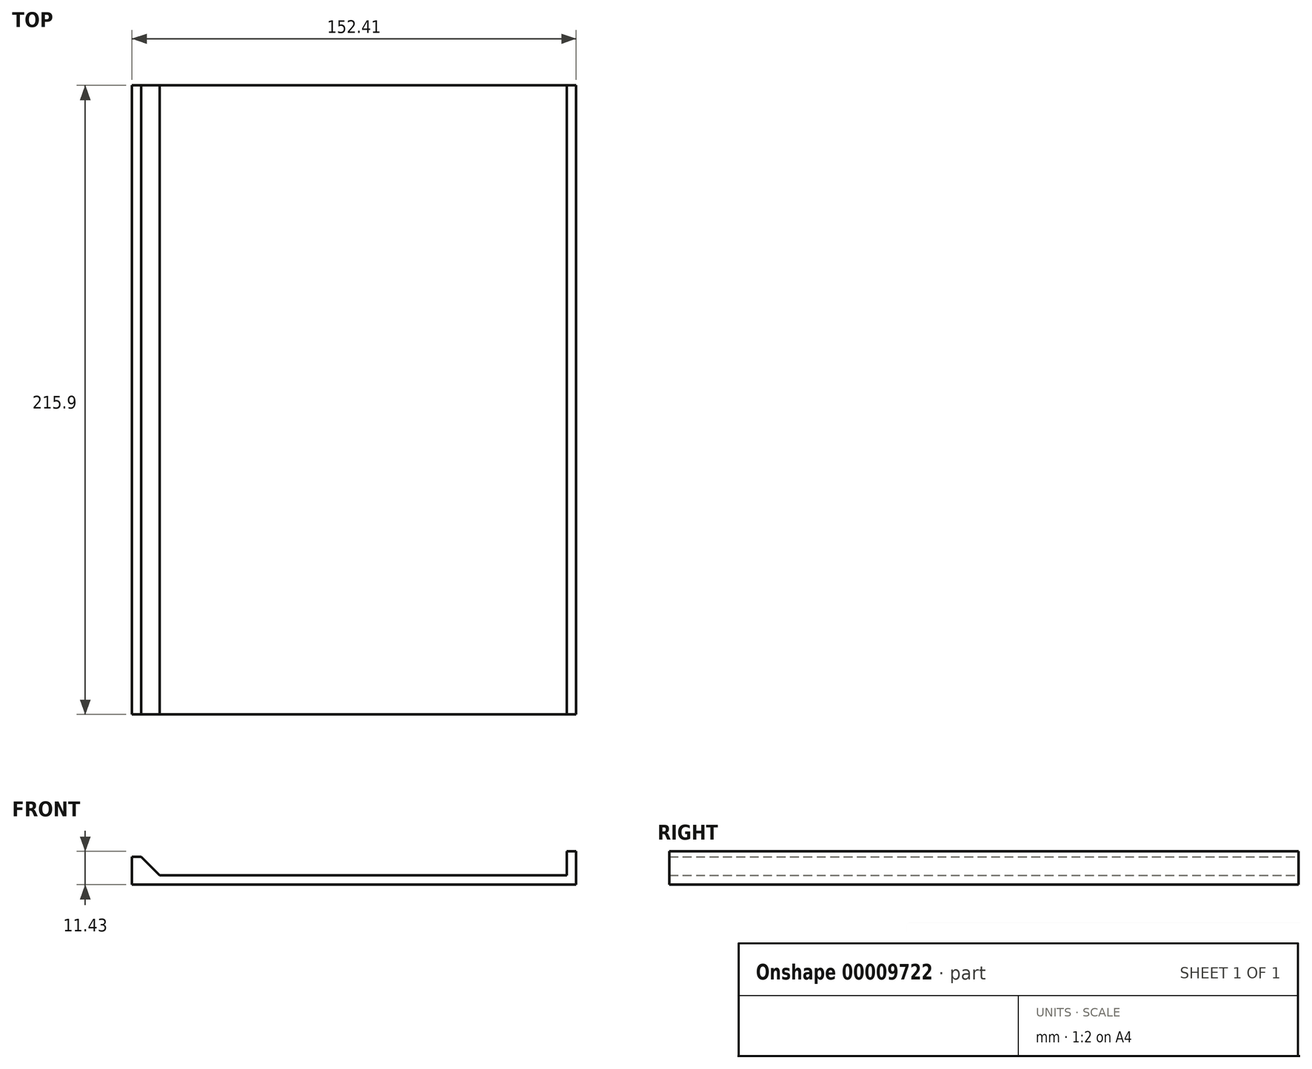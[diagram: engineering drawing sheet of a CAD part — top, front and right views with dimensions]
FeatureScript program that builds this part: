
annotation { "Feature Type Name" : "Feature", "Feature Type Description" : "" }
export const myFeature = defineFeature(function(context is Context, id is Id, definition is map)
    precondition{}
    {
        {
            var Q0;
            Q0=qCreatedBy(makeId("Front.planeOp"),FACE);
            var sketch = newSketch(context, id + "F0", { "sketchPlane" : qUnion([Q0])});
            skLineSegment(sketch, "E0", {"start": v(0, 0) * mm, "end": v(139.7, 0) * mm});
            skLineSegment(sketch, "E1", {"start": v(0, 0) * mm, "end": v(-6.35, 6.35) * mm});
            skLineSegment(sketch, "E2", {"start": v(-6.35, 6.35) * mm, "end": v(-9.53, 6.35) * mm});
            skLineSegment(sketch, "E3", {"start": v(-9.53, 6.35) * mm, "end": v(-9.53, -3.18) * mm});
            skLineSegment(sketch, "E4", {"start": v(-9.53, -3.18) * mm, "end": v(142.88, -3.17) * mm});
            skLineSegment(sketch, "E5", {"start": v(142.88, -3.17) * mm, "end": v(142.88, 8.26) * mm});
            skLineSegment(sketch, "E6", {"start": v(142.88, 8.26) * mm, "end": v(139.7, 8.26) * mm});
            skLineSegment(sketch, "E7", {"start": v(139.7, 8.26) * mm, "end": v(139.7, 0) * mm});
            skSolve(sketch);
        }
        {
            var Q0;
            Q0 = qSketchRegion(id + "F0", true);
            extrude(context, id + "F1", {"entities" : qUnion([Q0]), "endBound" : BoundingType.SYMMETRIC, "depth" : 215.9 * mm});
        }
    });
